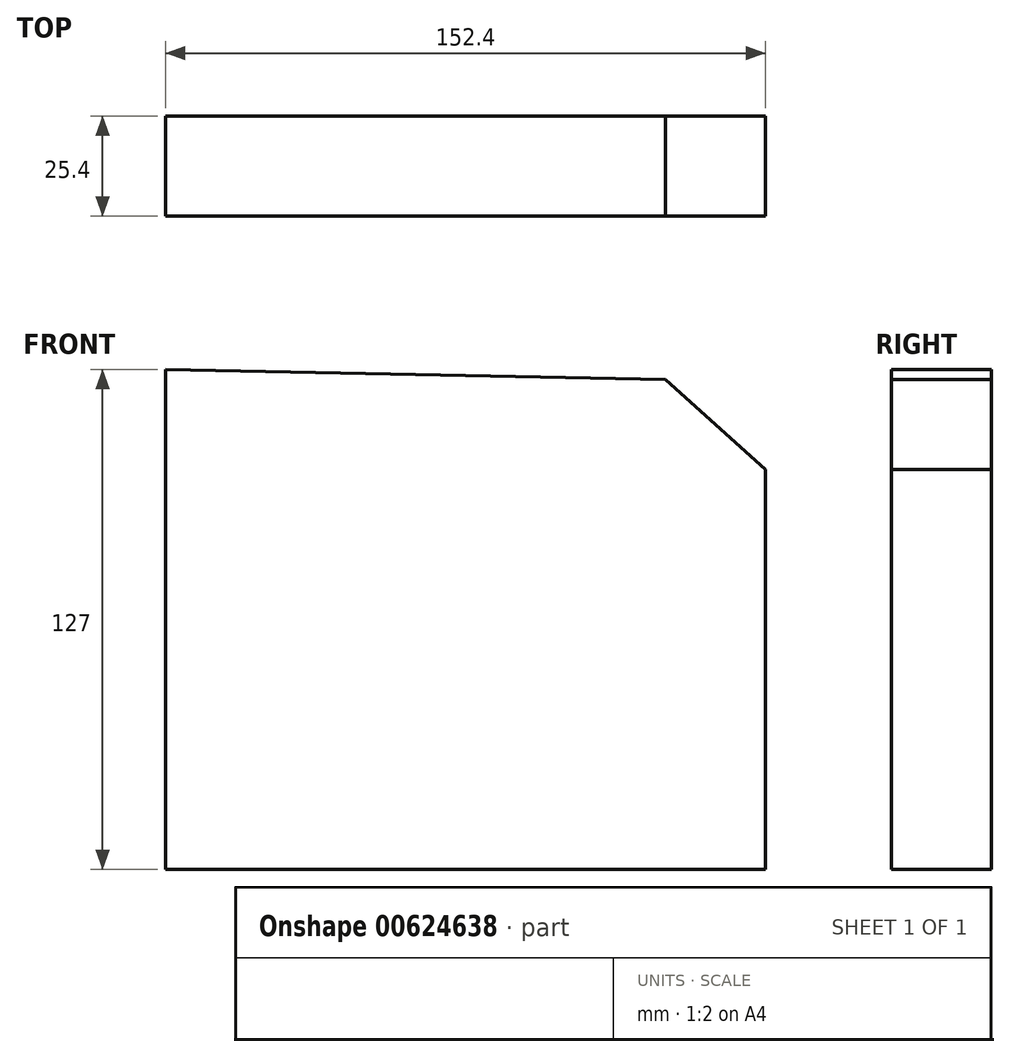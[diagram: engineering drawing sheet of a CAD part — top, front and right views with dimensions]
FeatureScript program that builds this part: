
annotation { "Feature Type Name" : "Feature", "Feature Type Description" : "" }
export const myFeature = defineFeature(function(context is Context, id is Id, definition is map)
    precondition{}
    {
        {
            var Q0;
            Q0=qCreatedBy(makeId("Front.planeOp"),FACE);
            var sketch = newSketch(context, id + "F0", { "sketchPlane" : qUnion([Q0])});
            skLineSegment(sketch, "E0", {"start": v(-107.25, 90.06) * mm, "end": v(-107.25, -36.94) * mm});
            skLineSegment(sketch, "E1", {"start": v(-107.25, -36.94) * mm, "end": v(45.15, -36.94) * mm});
            skLineSegment(sketch, "E2", {"start": v(45.15, -36.94) * mm, "end": v(45.15, 64.66) * mm});
            skLineSegment(sketch, "E3", {"start": v(45.15, 64.66) * mm, "end": v(19.72, 87.5) * mm});
            skLineSegment(sketch, "E4", {"start": v(19.72, 87.5) * mm, "end": v(-107.25, 90.06) * mm});
            skSolve(sketch);
        }
        {
            var Q0;
            Q0=makeQuery(id+"F0.imprint","IMPRINT",FACE,{"disambiguationData":[TD([[makeQuery(id+"F0.imprint","IMPRINT",EDGE,{"derivedFrom":sQuery(id+"F0.wireOp",EDGE,"E0")}),1.0]])]});
            extrude(context, id + "F1", {"entities" : qUnion([Q0]), "depth" : 25.4 * mm, "offsetDistance" : 25.4 * mm});
        }
    });
